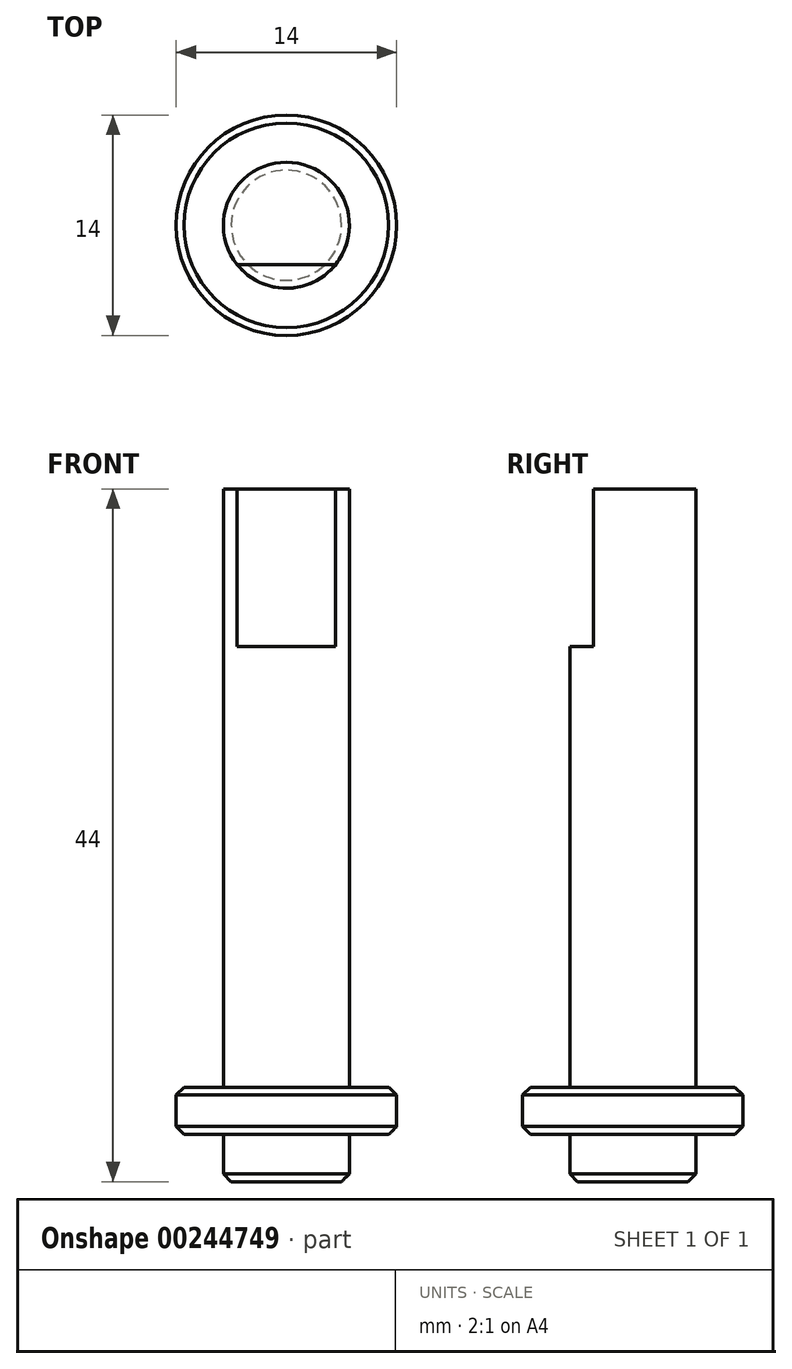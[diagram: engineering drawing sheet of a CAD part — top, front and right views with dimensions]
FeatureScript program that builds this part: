
annotation { "Feature Type Name" : "Feature", "Feature Type Description" : "" }
export const myFeature = defineFeature(function(context is Context, id is Id, definition is map)
    precondition{}
    {
        {
            var Q0;
            Q0=qCreatedBy(makeId("Top.planeOp"),FACE);
            var sketch = newSketch(context, id + "F0", { "sketchPlane" : qUnion([Q0])});
            skCircle(sketch, "E0", {"center": v(0, 0) * mm, "radius": 4 * mm});
            skCircle(sketch, "E1", {"center": v(0, 0) * mm, "radius": 7 * mm});
            skSolve(sketch);
        }
        {
            var Q0;
            Q0=makeQuery(id+"F0.imprint","IMPRINT",FACE,{"disambiguationData":[TD([[makeQuery(id+"F0.imprint","IMPRINT",EDGE,{"derivedFrom":sQuery(id+"F0.wireOp",EDGE,"E0")}),1.0]])]});
            extrude(context, id + "F1", {"entities" : qUnion([Q0]), "depth" : 41 * mm});
        }
        {
            var Q0;
            Q0=makeQuery(id+"F0.imprint","IMPRINT",FACE,{"disambiguationData":[TD([[makeQuery(id+"F0.imprint","IMPRINT",EDGE,{"derivedFrom":sQuery(id+"F0.wireOp",EDGE,"E0")}),1.0]])]});
            var Q1;
            Q1=sQuery(id+"F0.wireOp",EDGE,"E0");
            extrude(context, id + "F2", {"entities" : qUnion([Q0]), "operationType" : NewBodyOperationType.ADD, "surfaceEntities" : qUnion([Q1]), "oppositeDirection" : true, "depth" : 3 * mm});
        }
        {
            var Q0;
            Q0=makeQuery(id+"F0.imprint","IMPRINT",FACE,{"disambiguationData":[TD([[makeQuery(id+"F0.imprint","IMPRINT",EDGE,{"derivedFrom":sQuery(id+"F0.wireOp",EDGE,"E0")}),-1.0]])]});
            extrude(context, id + "F3", {"entities" : qUnion([Q0]), "operationType" : NewBodyOperationType.ADD, "depth" : 3 * mm});
        }
        {
            var Q0;
            Q0=makeQuery(id+"F1.opExtrude","CAP_FACE",FACE,{"disambiguationData":[OSD([sQuery(id+"F0.wireOp",EDGE,"E0")])],"isStart":false});
            var sketch = newSketch(context, id + "F4", { "sketchPlane" : qUnion([Q0])});
            skLineSegment(sketch, "E2", {"start": v(0, 0) * mm, "end": v(0, -2.5) * mm});
            skLineSegment(sketch, "E3.bottom", {"start": v(4.57, -2.5) * mm, "end": v(-4.51, -2.5) * mm});
            skLineSegment(sketch, "E3.top", {"start": v(4.57, -5.26) * mm, "end": v(-4.51, -5.26) * mm});
            skLineSegment(sketch, "E3.left", {"start": v(4.57, -2.5) * mm, "end": v(4.57, -5.26) * mm});
            skLineSegment(sketch, "E3.right", {"start": v(-4.51, -2.5) * mm, "end": v(-4.51, -5.26) * mm});
            skSolve(sketch);
        }
        {
            var Q0;
            Q0 = qSketchRegion(id + "F4", true);
            extrude(context, id + "F5", {"entities" : qUnion([Q0]), "operationType" : NewBodyOperationType.REMOVE, "oppositeDirection" : true, "depth" : 10 * mm});
        }
        {
            var Q0;
            Q0=makeQuery(id+"F3.opExtrude","CAP_EDGE",EDGE,{"disambiguationData":[OSD([sQuery(id+"F0.wireOp",EDGE,"E1")])],"isStart":false});
            chamfer(context, id + "F6", {"entities" : qUnion([Q0]), "chamferType" : ChamferType.OFFSET_ANGLE, "width" : .5 * mm, "oppositeDirection" : false, "angle" : 45 * degree, "tangentPropagation" : true});
        }
        {
            var Q0;
            Q0=makeQuery(id+"F3.opExtrude","CAP_EDGE",EDGE,{"disambiguationData":[OSD([sQuery(id+"F0.wireOp",EDGE,"E1")])],"isStart":true});
            chamfer(context, id + "F7", {"entities" : qUnion([Q0]), "chamferType" : ChamferType.OFFSET_ANGLE, "width" : .5 * mm, "oppositeDirection" : false, "angle" : 45 * degree, "tangentPropagation" : true});
        }
        {
            var Q0;
            Q0=makeQuery(id+"F2.opExtrude","CAP_EDGE",EDGE,{"disambiguationData":[OSD([sQuery(id+"F0.wireOp",EDGE,"E0")])],"isStart":false});
            chamfer(context, id + "F8", {"entities" : qUnion([Q0]), "chamferType" : ChamferType.OFFSET_ANGLE, "width" : .5 * mm, "oppositeDirection" : false, "angle" : 45 * degree, "tangentPropagation" : true});
        }
    });
